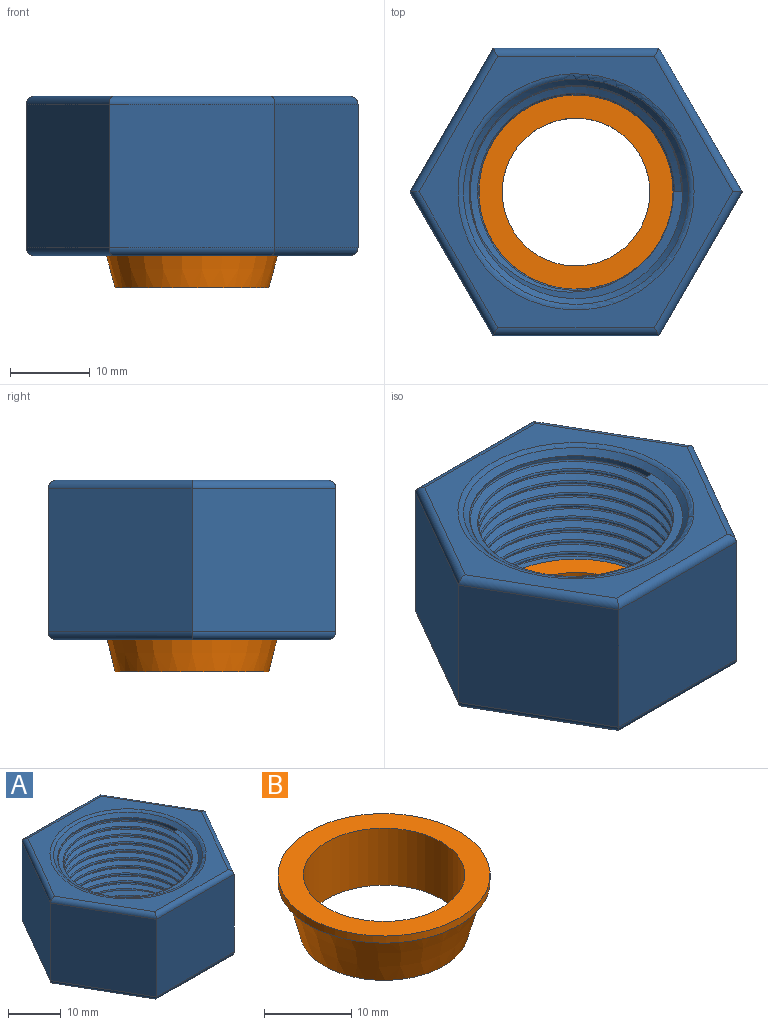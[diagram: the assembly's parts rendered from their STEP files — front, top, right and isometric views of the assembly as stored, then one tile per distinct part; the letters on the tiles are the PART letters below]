
ASSEMBLY  parts=2 mates=1
PART A: 32 faces, bbox 42x36.4x20.4 mm
  f0: cylinder r=13.35mm len=26.7mm, axis (0,0,-1), area 148.9mm2, adj f1,f2,f12,f16,f18
  f1: plane 1.14x0.8mm, normal (0,1,0), area 0.4mm2, adj f0,f4,f15,f16,f17
  f2: bspline ~30.83x26.7mm, area 199.5mm2, adj f0,f3,f12,f17
  f3: bspline ~30.52x26.43mm, area 712.4mm2, adj f2,f4,f12,f17
  f4: bspline ~28.46x24.65mm, area 368.1mm2, adj f1,f3,f12,f15,f17
  f5: plane 20.78x18mm, normal (0,-1,0), area 374.1mm2, adj f6,f10,f21,f29
  f6: plane 18x18mm, normal (0.87,-0.5,0), area 374.1mm2, adj f5,f7,f20,f27
  f7: plane 18x18mm, normal (0.87,0.5,0), area 374.1mm2, adj f6,f8,f22,f26
  f8: plane 20.78x18mm, normal (0,1,0), area 374.1mm2, adj f7,f9,f24,f28
  f9: plane 18x18mm, normal (-0.87,0.5,0), area 374.1mm2, adj f8,f10,f25,f30
  f10: plane 18x18mm, normal (-0.87,-0.5,0), area 374.1mm2, adj f5,f9,f23,f31
  f11: plane 39.26x34mm, normal (0,0,1), area 314mm2, adj f19,f26,f27,f28,f29,f30,f31
  f12: plane 26.03x26.01mm, normal (0,0,1), area 166.6mm2, adj f0,f2,f3,f4,f14,f15,f16
  f13: plane 39.26x34mm, normal (0,0,-1), area 705.8mm2, adj f14,f20,f21,f22,f23,f24,f25
  f14: cone r=10.5mm half-angle=15deg, axis (0,0,1), area 197.1mm2, adj f12,f13
  f15: bspline ~30.52x26.43mm, area 694.4mm2, adj f1,f4,f12,f16
  f16: bspline ~30.83x26.7mm, area 192.2mm2, adj f0,f1,f12,f15
  f17: plane 27.13x19.15mm, normal (0,0,1), area 29.6mm2, adj f1,f2,f3,f4,f18
  f18: cone r=13.35mm half-angle=46deg, axis (0,0,1), area 89.3mm2, adj f0,f17,f19
  f19: torus R=14.79mm, axis (0,0,1), area 69.6mm2, adj f11,f18
  f20: cylinder r=1mm len=18.5mm, axis (0.5,0.87,0), area 31.7mm2, adj f6,f13,f21,f22
  f21: cylinder r=1mm len=20.78mm, axis (1,0,0), area 31.7mm2, adj f5,f13,f20,f23
  f22: cylinder r=1mm len=18.5mm, axis (-0.5,0.87,0), area 31.7mm2, adj f7,f13,f20,f24
  f23: cylinder r=1mm len=18.5mm, axis (0.5,-0.87,0), area 31.7mm2, adj f10,f13,f21,f25
  f24: cylinder r=1mm len=20.78mm, axis (-1,0,0), area 31.7mm2, adj f8,f13,f22,f25
  f25: cylinder r=1mm len=18.5mm, axis (-0.5,-0.87,0), area 31.7mm2, adj f9,f13,f23,f24
  f26: cylinder r=1mm len=18.5mm, axis (0.5,-0.87,0), area 31.7mm2, adj f7,f11,f27,f28
  f27: cylinder r=1mm len=18.5mm, axis (-0.5,-0.87,0), area 31.7mm2, adj f6,f11,f26,f29
  f28: cylinder r=1mm len=20.78mm, axis (1,0,0), area 31.7mm2, adj f8,f11,f26,f30
  f29: cylinder r=1mm len=20.78mm, axis (-1,0,0), area 31.7mm2, adj f5,f11,f27,f31
  f30: cylinder r=1mm len=18.5mm, axis (0.5,0.87,0), area 31.7mm2, adj f9,f11,f28,f31
  f31: cylinder r=1mm len=18.5mm, axis (-0.5,0.87,0), area 31.7mm2, adj f10,f11,f29,f30
PART B: 6 faces, bbox 24.3x24.3x8 mm
  f0: cylinder r=12.15mm len=24.3mm, axis (0,0,-1), area 76.3mm2, adj f2,f3
  f1: cylinder r=9.25mm len=18.5mm, axis (0,0,-1), area 465mm2, adj f2,f4
  f2: plane 24.3x24.3mm, normal (0,0,1), area 195mm2, adj f0,f1
  f3: plane 24.3x24.3mm, normal (0,0,-1), area 48.3mm2, adj f0,f5
  f4: plane 19.25x19.25mm, normal (0,0,-1), area 22.2mm2, adj f1,f5
  f5: cone r=11.5mm half-angle=15deg, axis (0,0,1), area 480.9mm2, adj f3,f4
PLACE A t=(-3.13,-0.28,-4.72)mm fixed
PLACE B t=(-3.13,-0.28,-4.72)mm
MATE slider B.f0 <-> A.f14  axis (0,0,-1) through (-3.13,-0.28,-4.72)mm
